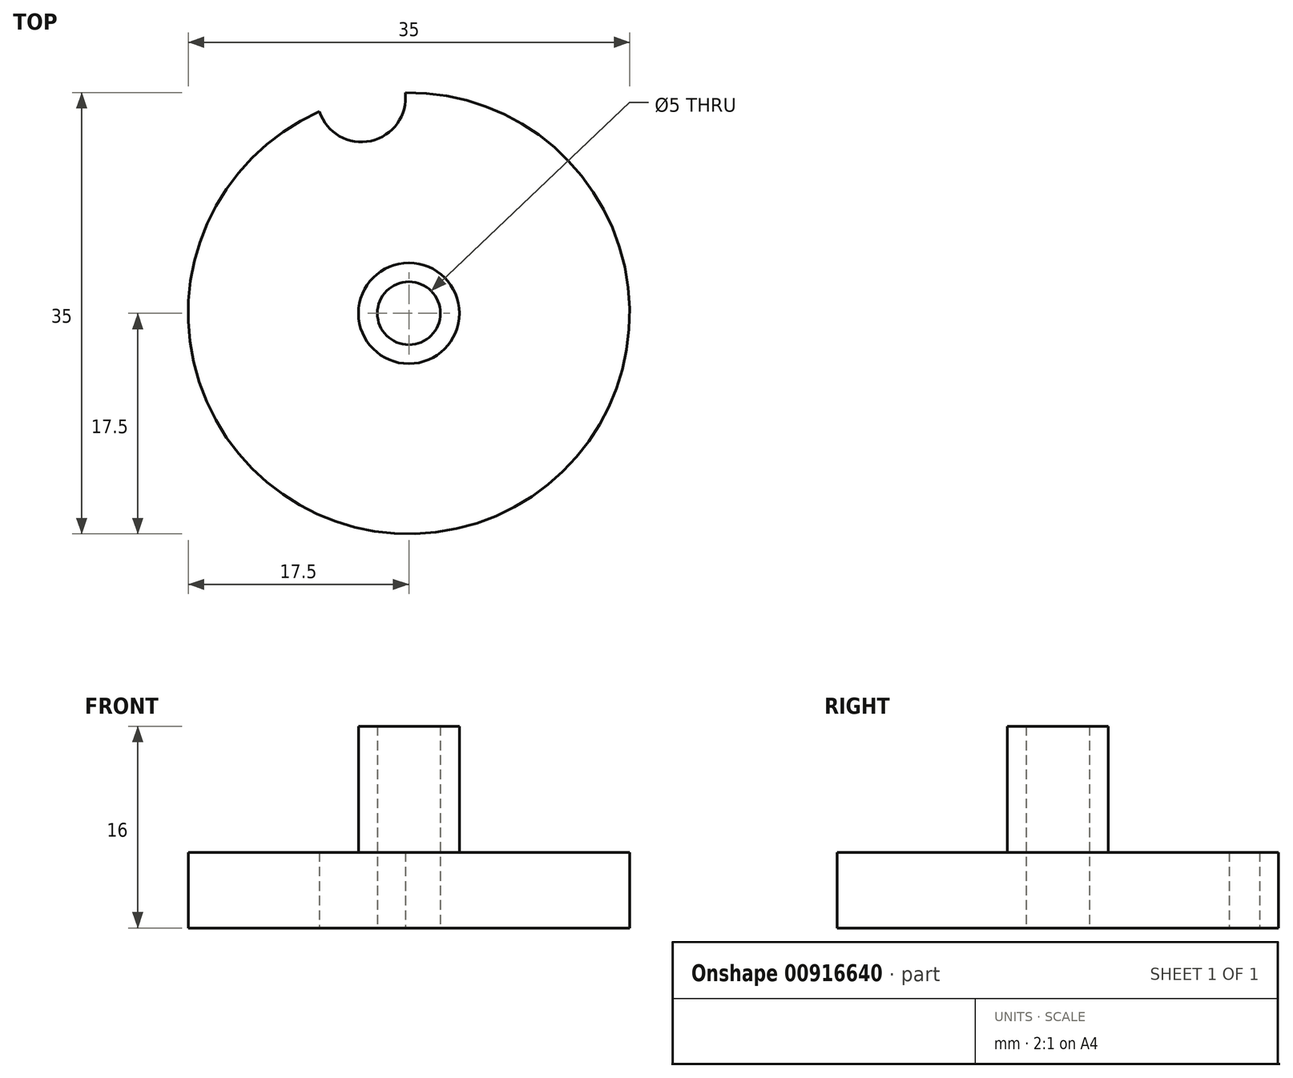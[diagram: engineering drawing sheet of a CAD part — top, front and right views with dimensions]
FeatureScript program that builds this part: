
annotation { "Feature Type Name" : "Feature", "Feature Type Description" : "" }
export const myFeature = defineFeature(function(context is Context, id is Id, definition is map)
    precondition{}
    {
        {
            var Q0;
            Q0=qCreatedBy(makeId("Top.planeOp"),FACE);
            var sketch = newSketch(context, id + "F0", { "sketchPlane" : qUnion([Q0])});
            skCircle(sketch, "E0", {"center": v(0, 0) * mm, "radius": 2.5 * mm});
            skCircle(sketch, "E1", {"center": v(0, 0) * mm, "radius": 17.5 * mm});
            skCircle(sketch, "E2", {"center": v(0, 0) * mm, "radius": 14 * mm, "construction": true});
            skCircle(sketch, "E3", {"center": v(-3.77, 17.09) * mm, "radius": 3.5 * mm});
            skSolve(sketch);
        }
        {
            var Q0;
            Q0=makeQuery(id+"F0.imprint","IMPRINT",FACE,{"disambiguationData":[TD([[makeQuery(id+"F0.imprint","IMPRINT",EDGE,{"derivedFrom":sQuery(id+"F0.wireOp",EDGE,"E0")}),-1.0]])]});
            extrude(context, id + "F1", {"entities" : qUnion([Q0]), "depth" : 6 * mm, "offsetDistance" : 25 * mm});
        }
        {
            var Q0;
            Q0=makeQuery(id+"F1.opExtrude","CAP_FACE",FACE,{"disambiguationData":[OSD([sQuery(id+"F0.wireOp",EDGE,"E0"),sQuery(id+"F0.wireOp",EDGE,"E1")])],"isStart":false});
            var sketch = newSketch(context, id + "F2", { "sketchPlane" : qUnion([Q0])});
            skCircle(sketch, "E4", {"center": v(0, 0) * mm, "radius": 4 * mm});
            skSolve(sketch);
        }
        {
            var Q0;
            Q0=makeQuery(id+"F2.imprint","IMPRINT",FACE,{"disambiguationData":[TD([[makeQuery(id+"F2.imprint","IMPRINT",EDGE,{"derivedFrom":sQuery(id+"F2.wireOp",EDGE,"E4")}),1.0]])]});
            extrude(context, id + "F3", {"entities" : qUnion([Q0]), "operationType" : NewBodyOperationType.ADD, "depth" : 10 * mm, "offsetDistance" : 25 * mm});
        }
    });
